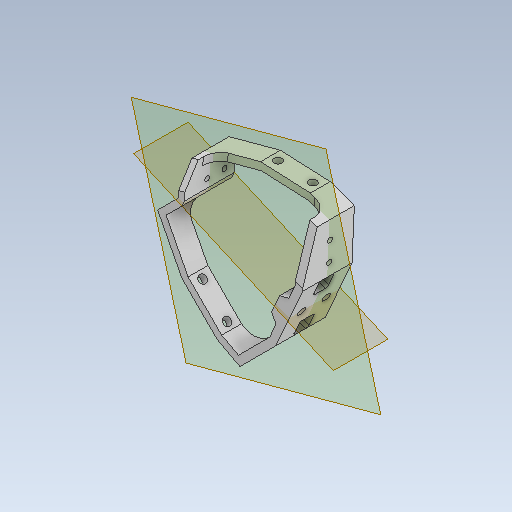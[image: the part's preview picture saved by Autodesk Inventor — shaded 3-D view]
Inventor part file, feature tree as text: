
AUTODESK INVENTOR PART (.ipt)
format: ipt  version: 2023 (Build 270158000, 158)  size: 520,192 bytes
history: native  units: mm
features: sketch x15, reference x15, thicken_offset x14, projected_geometry x13, extrude x11, other x7, plane x4, hole x4, chamfer x4, fillet x2
ambient origin geometry x8: Origin, YZ Plane, XZ Plane, XY Plane, X Axis, Y Axis, Z Axis, Center Point
bodies: Body1 (feature_tree)
feature tree (89):
  sketch  "Sketch1"  dims[d0=3.0mm d1=3.0mm]
  plane  "Work Plane1"
  plane  "Work Plane2"
  extrude  "Extrusion4"  Depth=3.0mm
  hole  "Hole1"  [1 undecoded]
  hole  "Hole2"  [1 undecoded]
  thicken_offset  "Thicken1"
  thicken_offset  "Thicken2"
  extrude  "Extrusion5"  Depth=10.0mm TaperAngle=0.0deg
  hole  "Hole3"  [1 undecoded]
  hole  "Hole4"  [1 undecoded]
  extrude  "Extrusion6"  Depth=2.5mm
  thicken_offset  "Thicken3"
  thicken_offset  "Thicken4"
  extrude  "Extrusion7"  Depth=10.0mm TaperAngle=0.0deg
  extrude  "Extrusion8"  Depth=3.0mm
  thicken_offset  "Thicken5"
  thicken_offset  "Thicken6"
  extrude  "Extrusion9"  Depth=4.0mm
  extrude  "Extrusion10"  Depth=4.0mm
  extrude  "Extrusion11"  Depth=3.0mm
  fillet  "Fillet2"  Radius=3.5mm
  thicken_offset  "Thicken7"
  thicken_offset  "Thicken8"
  chamfer  "Chamfer2"  Distance=1.0mm
  chamfer  "Chamfer3"  Distance=7.0mm
  chamfer  "Chamfer4"  Distance=7.0mm
  chamfer  "Chamfer5"  Distance=4.0mm
  extrude  "Extrusion14"  Depth=4.0mm
  extrude  "Extrusion15"  Depth=1.0mm
  plane  "Work Plane3"
  extrude  "Extrusion16"  Depth=1.0mm
  fillet  "Fillet4"  Radius=3.5mm
  thicken_offset  "Thicken9"
  thicken_offset  "Thicken10"
  thicken_offset  "Thicken11"
  thicken_offset  "Thicken12"
  thicken_offset  "Thicken13"
  thicken_offset  "Thicken14"
  plane  "Work Plane4"
  reference  "Reference1"
  reference  "Reference2"
  sketch  "Sketch4"  dims[d2=3.0mm d3=3.0mm]
  reference  "Reference7"
  reference  "Reference8"
  sketch  "Sketch5"  dims[d4=3.0mm d5=3.0mm]
  reference  "Reference9"
  reference  "Reference10"
  sketch  "Sketch6"  dims[d6=3.0mm d15=10.0mm d16=0.0mm]
  reference  "Reference11"
  reference  "Reference12"
  sketch  "Sketch7"  dims[d17=2.0mm d18=6.0mm d19=4.0mm d20=2.0mm d21=90.0deg d22=5.0mm d23=0.0mm]
  reference  "Reference13"
  reference  "Reference14"
  sketch  "Sketch8"  dims[d24=2.0mm d25=6.0mm d26=4.0mm d27=2.0mm d28=90.0deg d29=5.0mm d30=0.0mm d31=1.0mm]
  reference  "Reference15"
  reference  "Reference16"
  sketch  "Sketch10"  dims[d32=1.0mm d33=1.0mm]
  projected_geometry  "Projected Loop1"
  sketch  "Sketch11"  dims[d34=1.0mm d35=2.5mm]
  projected_geometry  "Projected Loop2"
  projected_geometry  "Projected Loop3"
  reference  "Reference19"
  reference  "Reference20"
  sketch  "Sketch12"  dims[d36=2.5mm d39=10.0mm d40=0.0mm]
  projected_geometry  "Projected Loop4"
  projected_geometry  "Projected Loop5"
  projected_geometry  "Projected Loop6"
  sketch  "Sketch13"  dims[d41=2.0mm d42=6.0mm d43=4.0mm d44=2.0mm d45=90.0deg d46=5.0mm d47=0.0mm]
  projected_geometry  "Projected Loop7"
  projected_geometry  "Projected Loop8"
  reference  "Reference21"
  sketch  "Sketch14"  dims[d48=2.0mm d49=6.0mm d50=4.0mm d51=2.0mm d52=90.0deg d53=5.0mm d54=0.0mm d60=3.0mm]
  projected_geometry  "Projected Loop9"
  sketch  "Sketch15"  dims[d61=4.0mm d62=4.0mm]
  projected_geometry  "Projected Loop10"
  sketch  "Sketch18"  dims[d63=10.0mm d64=0.0mm d65=4.0mm d66=3.0mm]
  projected_geometry  "Projected Loop13"
  sketch  "Sketch19"  dims[d67=4.5mm d68=3.0mm d69=3.5mm d70=3.5mm]
  projected_geometry  "Projected Loop14"
  sketch  "Sketch20"  dims[d71=3.5mm d72=1.0mm d73=7.0mm d74=0.0mm d75=7.0mm d76=0.0mm d79=4.0mm d80=4.0mm d81=4.5mm d82=4.5mm d83=3.5mm d84=3.5mm d85=1.0mm d86=3.5mm d87=7.0mm d88=0.0mm d89=7.0mm d90=0.0mm d91=5.0mm d92=5.0mm d93=3.2mm d94=3.2mm d95=7.0mm d96=0.0mm d100=5.0mm d114=1.0mm d115=1.0mm d116=1.0mm d117=1.0mm d118=5.0mm d119=2.0mm d120=75.0deg d121=5.0mm d122=2.0mm d123=75.0deg d124=5.0mm d125=2.0mm d126=60.0deg d127=5.0mm d128=2.0mm d129=60.0deg d130=7.0mm d131=7.0mm d132=3.2mm d133=3.2mm d134=7.0mm d135=0.0mm d136=7.0mm d137=7.0mm d138=3.2mm d139=3.2mm d140=7.0mm d141=0.0mm d142=7.0mm d143=6.0mm d145=7.0mm d146=6.0mm d147=10.0mm d148=0.0mm d149=1.0mm d150=0.5mm d151=0.5mm d152=0.5mm d153=0.5mm d154=0.5mm d155=0.5mm d156=0.5mm d157=0.5mm d158=0.5mm d159=0.5mm d160=0.5mm d161=0.5mm]
  projected_geometry  "Projected Loop15"
  parser-record x1  (decoder bookkeeping rows leaked as tree rows — omitted from the tree; the rows remain in map.json)
  other  "leg_1.iam"
  other  "reducer_1:1"
  other  "mot_holder_1:1"
  other  "reducer_1:2"
  other  "screw_holder_2_3:6"
  other  "screw_holder_2_3:7"
note: 4 required parameter values undecoded (feature->parameter linkage not recoverable at this tier; creation-order binding heuristic only, values carry confidence <= 0.55)
note: 1 file-system path scrubbed to <path> (originals preserved in map.json)
